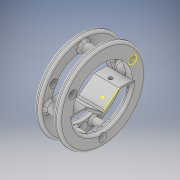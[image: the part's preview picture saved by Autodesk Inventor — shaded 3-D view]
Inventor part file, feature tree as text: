
AUTODESK INVENTOR PART (.ipt)
format: ipt  version: 2019 (Build 230136000, 136)  size: 692,224 bytes
history: native  units: in
note: dims shown in document units (in); Inventor stores cm internally (conversion verified against a paired STEP export)
features: sketch x9, fillet x9, extrude x7, mirror x2, projected_geometry x2, plane x1, pattern_circular x1
ambient origin geometry x8: Origin, YZ Plane, XZ Plane, XY Plane, X Axis, Y Axis, Z Axis, Center Point
bodies: Solid1 (feature_tree)
feature tree (31):
  extrude  "Extrusion1"  Depth=0.4331in
  extrude  "Extrusion2"  Depth=0.3937in
  mirror  "Mirror1"
  extrude  "Extrusion3"  Depth=0.5118in
  plane  "Work Plane1"
  extrude  "Extrusion4"  Depth=0.1181in
  extrude  "Extrusion5"  Depth=0.7874in TaperAngle=0.0deg
  pattern_circular  "Circular Pattern1"  Count=2  [1 undecoded]
  extrude  "Extrusion6"  Depth=0.1969in TaperAngle=0.0deg
  extrude  "Extrusion7"  Depth=0.2441in
  mirror  "Mirror2"
  sketch  "Sketch12"  dims[d47=0.122in]
  sketch  "Sketch14"  dims[d48=0.1969in d49=0.0in d50=0.4724in d51=0.0787in d52=90.0deg d53=0.122in d55=0.0787in d56=0.0787in d57=0.0591in d58=0.0787in d59=0.0787in d60=0.0787in d61=0.0787in d62=0.0787in d63=0.0787in]
  fillet  "Fillet2"  Radius=0.7874in
  fillet  "Fillet3"  Radius=1.1811in
  fillet  "Fillet4"  Radius=2.1654in
  fillet  "Fillet5"  Radius=0.2756in
  fillet  "Fillet6"  Radius=0.1969in
  fillet  "Fillet7"  Radius=0.1969in
  fillet  "Fillet8"  Radius=0.2756in
  fillet  "Fillet9"  Radius=0.2756in
  fillet  "Fillet10"  Radius=0.7874in
  sketch  "Sketch2"  dims[d4=2.7165in d5=0.4331in]
  sketch  "Sketch4"  dims[d6=0.1969in d7=0.0in d16=0.3937in]
  sketch  "Sketch5"  dims[d17=0.5118in d18=0.3603in]
  projected_geometry  "Projected Loop1"
  sketch  "Sketch6"  dims[d20=0.1181in d21=0.1181in]
  projected_geometry  "Projected Loop2"
  sketch  "Sketch9"  dims[d22=180.0deg d23=0.7874in d24=0.0in d25=0.7874in d26=0.0in]
  sketch  "Sketch10"  dims[d27=-0.7874in d28=0.1969in d29=0.0in]
  sketch  "Sketch11"  dims[d32=2.1654in d33=0.2441in d34=0.7874in d35=0.0in d36=1.1811in d37=360.0deg d39=2.1654in d40=0.2756in d41=0.1969in d42=0.1969in d43=0.2756in d44=0.2756in d45=0.7874in d46=0.0in]
note: 1 required parameter value undecoded (feature->parameter linkage not recoverable at this tier; creation-order binding heuristic only, values carry confidence <= 0.55)
